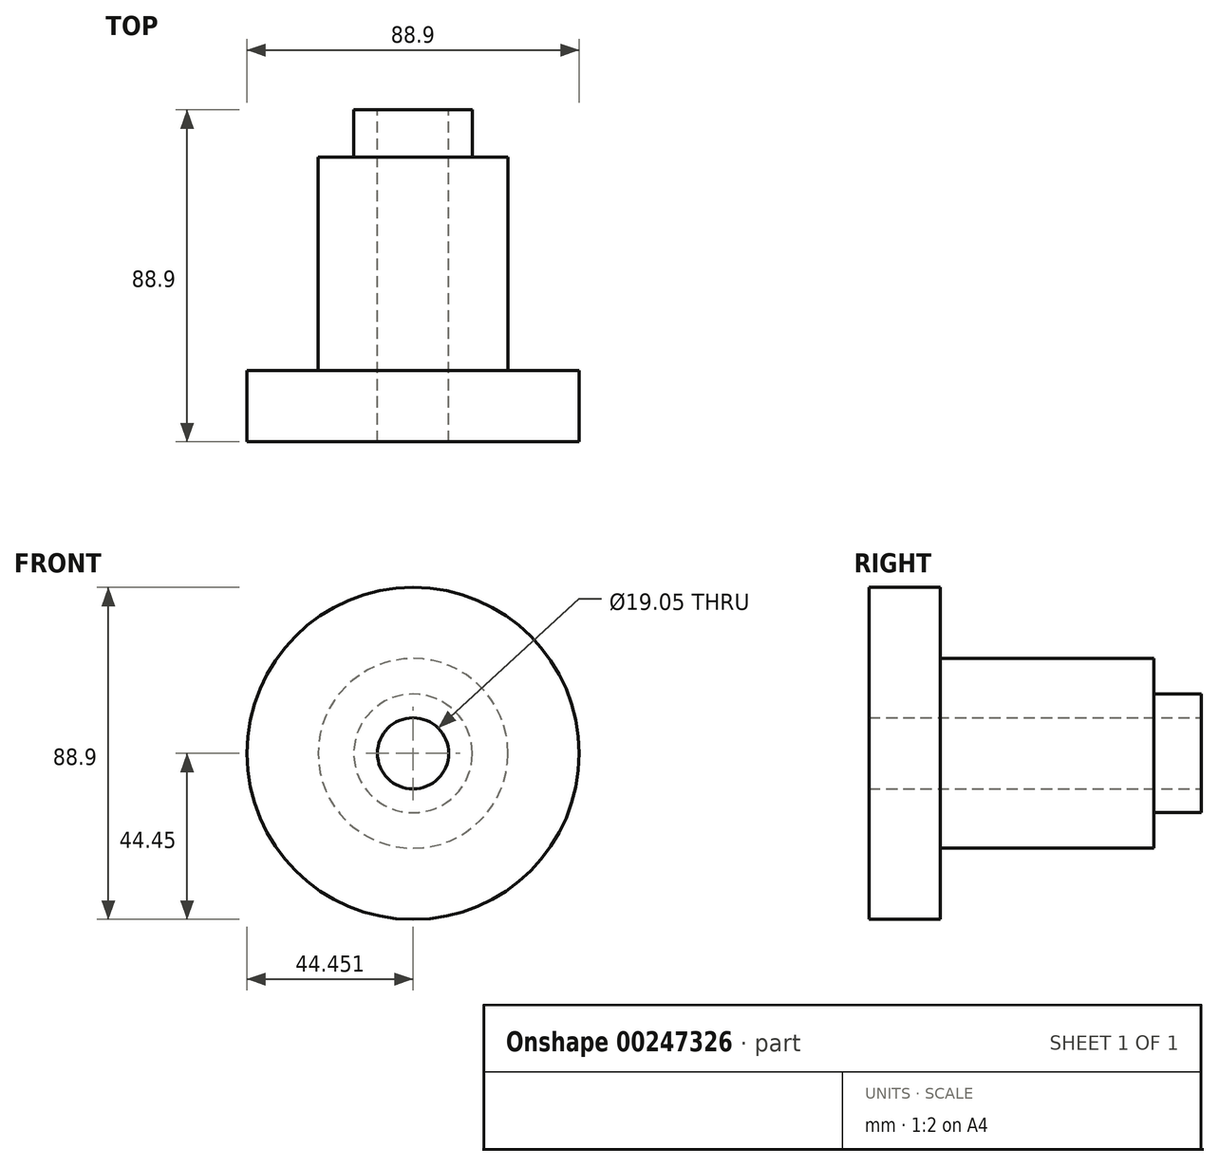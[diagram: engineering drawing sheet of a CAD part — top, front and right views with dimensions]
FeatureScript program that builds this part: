
annotation { "Feature Type Name" : "Feature", "Feature Type Description" : "" }
export const myFeature = defineFeature(function(context is Context, id is Id, definition is map)
    precondition{}
    {
        {
            var Q0;
            Q0=qCreatedBy(makeId("Top.planeOp"),FACE);
            var sketch = newSketch(context, id + "F0", { "sketchPlane" : qUnion([Q0])});
            skLineSegment(sketch, "E0.bottom", {"start": v(-5.96, 58.82) * mm, "end": v(13.09, 58.82) * mm});
            skLineSegment(sketch, "E0.top", {"start": v(-5.96, -30.08) * mm, "end": v(13.09, -30.08) * mm});
            skLineSegment(sketch, "E0.left", {"start": v(-5.96, 58.82) * mm, "end": v(-5.96, -30.08) * mm});
            skLineSegment(sketch, "E0.right", {"start": v(13.09, 58.82) * mm, "end": v(13.09, -30.08) * mm});
            skPoint(sketch, "E1.firstSnap0", {"position": v(3.56, -30.08) * mm});
            skLineSegment(sketch, "E1.bottom", {"start": v(-40.89, -30.08) * mm, "end": v(48.01, -30.08) * mm});
            skLineSegment(sketch, "E1.top", {"start": v(-40.89, -11.03) * mm, "end": v(48.01, -11.03) * mm});
            skLineSegment(sketch, "E1.left", {"start": v(-40.89, -30.08) * mm, "end": v(-40.89, -11.03) * mm});
            skLineSegment(sketch, "E1.right", {"start": v(48.01, -30.08) * mm, "end": v(48.01, -11.03) * mm});
            skLineSegment(sketch, "E2.bottom", {"start": v(-21.84, -11.03) * mm, "end": v(28.96, -11.03) * mm});
            skLineSegment(sketch, "E2.top", {"start": v(-21.84, 46.12) * mm, "end": v(28.96, 46.12) * mm});
            skLineSegment(sketch, "E2.left", {"start": v(-21.84, -11.03) * mm, "end": v(-21.84, 46.12) * mm});
            skLineSegment(sketch, "E2.right", {"start": v(28.96, -11.03) * mm, "end": v(28.96, 46.12) * mm});
            skLineSegment(sketch, "E3.bottom", {"start": v(-12.31, 46.12) * mm, "end": v(19.44, 46.12) * mm});
            skLineSegment(sketch, "E3.top", {"start": v(-12.31, 58.82) * mm, "end": v(19.44, 58.82) * mm});
            skLineSegment(sketch, "E3.left", {"start": v(-12.31, 46.12) * mm, "end": v(-12.31, 58.82) * mm});
            skLineSegment(sketch, "E3.right", {"start": v(19.44, 46.12) * mm, "end": v(19.44, 58.82) * mm});
            skLineSegment(sketch, "E4", {"start": v(3.56, 58.82) * mm, "end": v(3.56, -30.08) * mm});
            skSolve(sketch);
        }
        {
            var Q0;
            {var subQ0=sQuery(id+"F0.wireOp",EDGE,"E2.left");Q0=makeQuery(id+"F0.imprint","IMPRINT",FACE,{"disambiguationData":[TD([[makeQuery(id+"F0.imprint","IMPRINT",EDGE,{"derivedFrom":subQ0}),-1.0]])]});}
            var Q1;
            {var subQ0=sQuery(id+"F0.wireOp",EDGE,"E1.left");Q1=makeQuery(id+"F0.imprint","IMPRINT",FACE,{"disambiguationData":[TD([[makeQuery(id+"F0.imprint","IMPRINT",EDGE,{"derivedFrom":subQ0}),-1.0]])]});}
            var Q2;
            {var subQ5=sQuery(id+"F0.wireOp",EDGE,"E3.left");Q2=makeQuery(id+"F0.imprint","IMPRINT",FACE,{"disambiguationData":[TD([[makeQuery(id+"F0.imprint","IMPRINT",EDGE,{"derivedFrom":subQ5}),-1.0]])]});}
            var Q3;
            Q3=sQuery(id+"F0.wireOp",EDGE,"E4");
            revolve(context, id + "F1", {"entities" : qUnion([Q0, Q1, Q2]), "axis" : qUnion([Q3]), "revolveType" : RevolveType.FULL});
        }
    });
